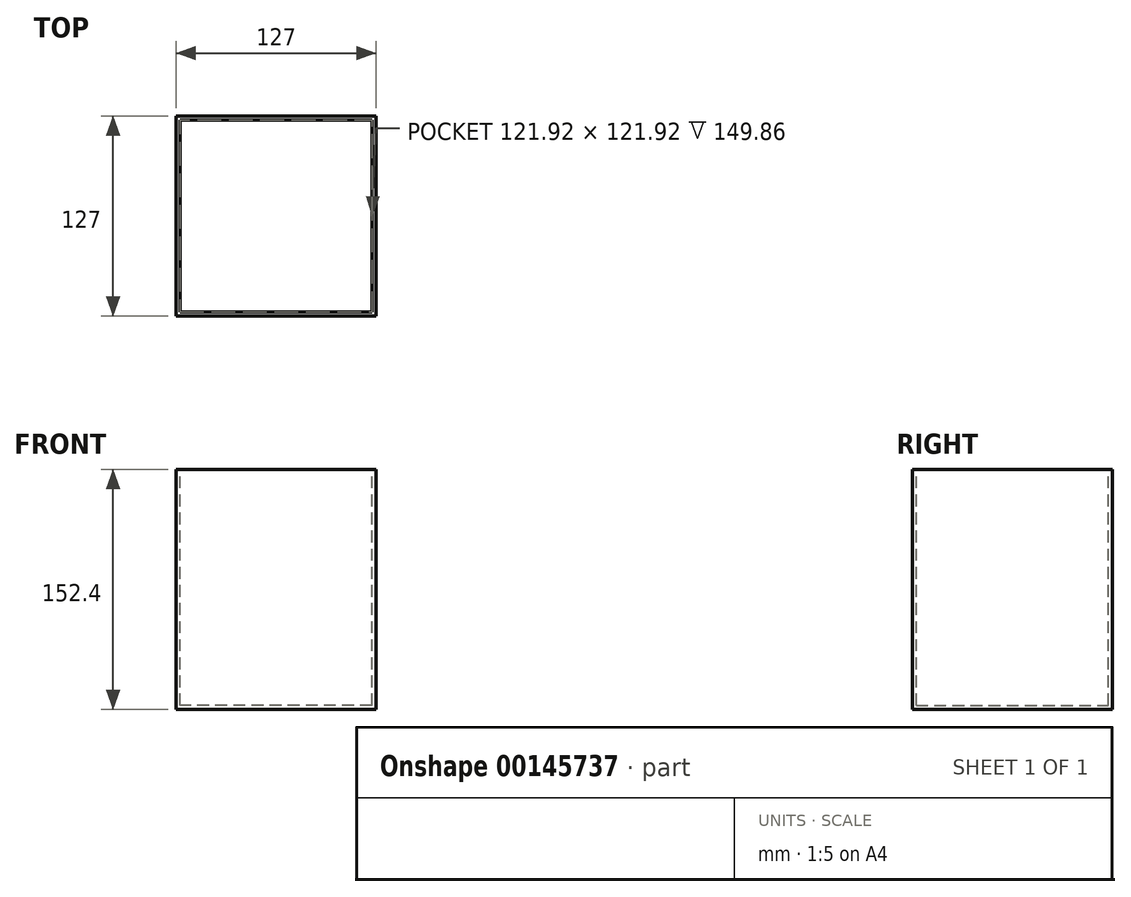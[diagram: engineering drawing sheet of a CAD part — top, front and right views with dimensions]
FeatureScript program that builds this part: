
annotation { "Feature Type Name" : "Feature", "Feature Type Description" : "" }
export const myFeature = defineFeature(function(context is Context, id is Id, definition is map)
    precondition{}
    {
        {
            var Q0;
            Q0=qCreatedBy(makeId("Front.planeOp"),FACE);
            var sketch = newSketch(context, id + "F0", { "sketchPlane" : qUnion([Q0])});
            skLineSegment(sketch, "E0.bottom", {"start": v(0, 0) * mm, "end": v(0, 0) * mm});
            skLineSegment(sketch, "E1.bottom", {"start": v(-6.93, 0) * mm, "end": v(-133.93, 0) * mm});
            skLineSegment(sketch, "E1.top", {"start": v(-6.93, 152.4) * mm, "end": v(-133.93, 152.4) * mm});
            skLineSegment(sketch, "E1.left", {"start": v(-6.93, 0) * mm, "end": v(-6.93, 152.4) * mm});
            skLineSegment(sketch, "E1.right", {"start": v(-133.93, 0) * mm, "end": v(-133.93, 152.4) * mm});
            skSolve(sketch);
        }
        {
            var Q0;
            Q0=makeQuery(id+"F0.imprint","IMPRINT",FACE,{"disambiguationData":[TD([[makeQuery(id+"F0.imprint","IMPRINT",EDGE,{"derivedFrom":sQuery(id+"F0.wireOp",EDGE,"E1.bottom")}),-1.0]])]});
            extrude(context, id + "F1", {"entities" : qUnion([Q0]), "depth" : 127 * mm});
        }
        {
            var Q0;
            Q0=makeQuery(id+"F1.opExtrude","SWEPT_FACE",FACE,{"disambiguationData":[OSD([sQuery(id+"F0.wireOp",EDGE,"E1.top")])]});
            shell(context, id + "F2", {"entities" : qUnion([Q0]), "thickness" : 2.54 * mm});
        }
    });
